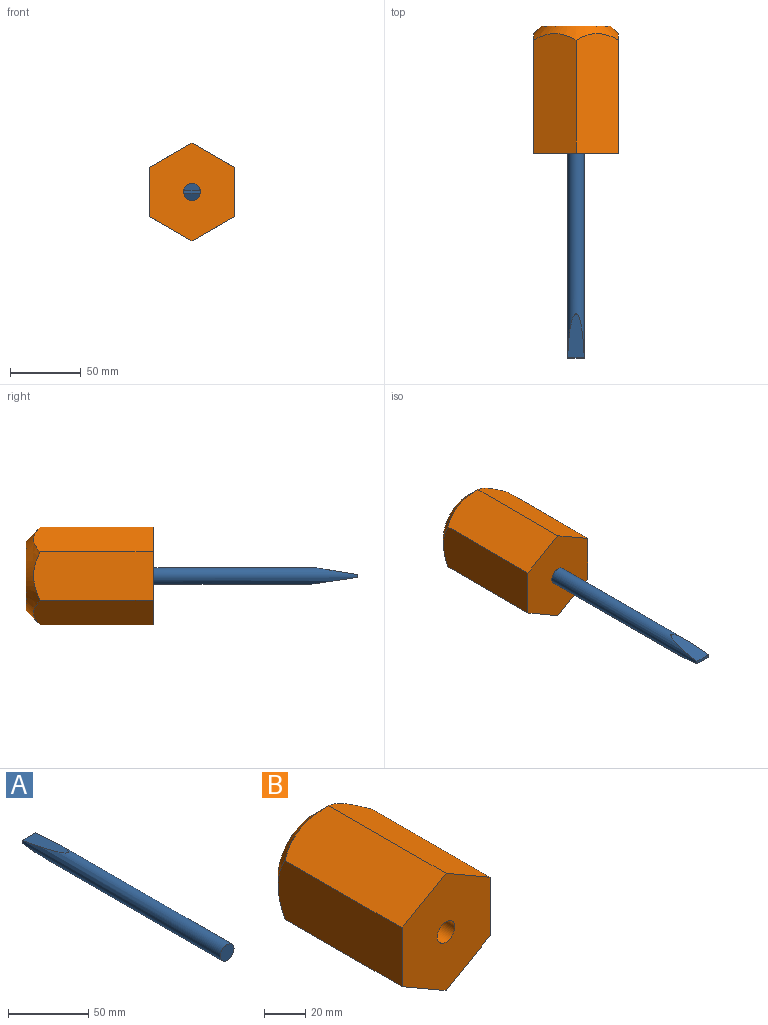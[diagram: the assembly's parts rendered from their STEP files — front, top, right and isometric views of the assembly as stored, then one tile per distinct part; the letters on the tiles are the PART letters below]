
ASSEMBLY  parts=2 mates=1
PART A: 5 faces, bbox 12x175x12 mm
  f0: cylinder r=6mm len=175mm, axis (0,-1,0), area 5886.5mm2, adj f1,f2,f3,f4
  f1: plane 12x2.05mm, normal (0,1,0), area 24.5mm2, adj f0,f3,f4
  f2: plane 12x12mm, normal (0,-1,0), area 113.1mm2, adj f0
  f3: plane 31.31x11.81mm, normal (0,0.16,-0.99), area 281.6mm2, adj f0,f1
  f4: plane 34.49x11.84mm, normal (0,0.14,0.99), area 311.2mm2, adj f0,f1
PART B: 11 faces, bbox 69.3x90x69.3 mm
  f0: plane 84.65x30mm, normal (-0.5,0,-0.87), area 2876.9mm2, adj f1,f5,f6,f7
  f1: plane 84.65x30mm, normal (0.5,0,-0.87), area 2876.9mm2, adj f0,f2,f6,f7
  f2: plane 84.65x34.66mm, normal (1,0,0), area 2876.9mm2, adj f1,f3,f6,f7
  f3: plane 84.65x30mm, normal (0.5,0,0.87), area 2876.9mm2, adj f2,f4,f6,f7
  f4: plane 84.65x30mm, normal (-0.5,0,0.87), area 2876.9mm2, adj f3,f5,f6,f7
  f5: plane 84.65x34.66mm, normal (-1,0,0), area 2876.9mm2, adj f0,f4,f6,f7
  f6: plane 69.28x60mm, normal (0,-1,0), area 3004.6mm2, adj f0,f1,f2,f3,f4,f5,f9
  f7: cone r=24.64mm half-angle=45deg, axis (0,-1,0), area 1711.5mm2, adj f0,f1,f2,f3,f4,f5,f8
  f8: plane 49.28x49.28mm, normal (0,1,0), area 1907.5mm2, adj f7
  f9: cylinder r=6mm len=30mm, axis (0,-1,0), area 1131mm2, adj f6,f10
  f10: plane 12x12mm, normal (0,-1,0), area 113.1mm2, adj f9
PLACE A rot(axis=(-1,0,0),180deg) t=(-16.63,35.88,-23.82)mm
PLACE B t=(-16.63,120.88,-23.82)mm
MATE planar B.f9 <-> A.f0  axis (0,-1,0) through (-16.63,60.88,-23.82)mm
